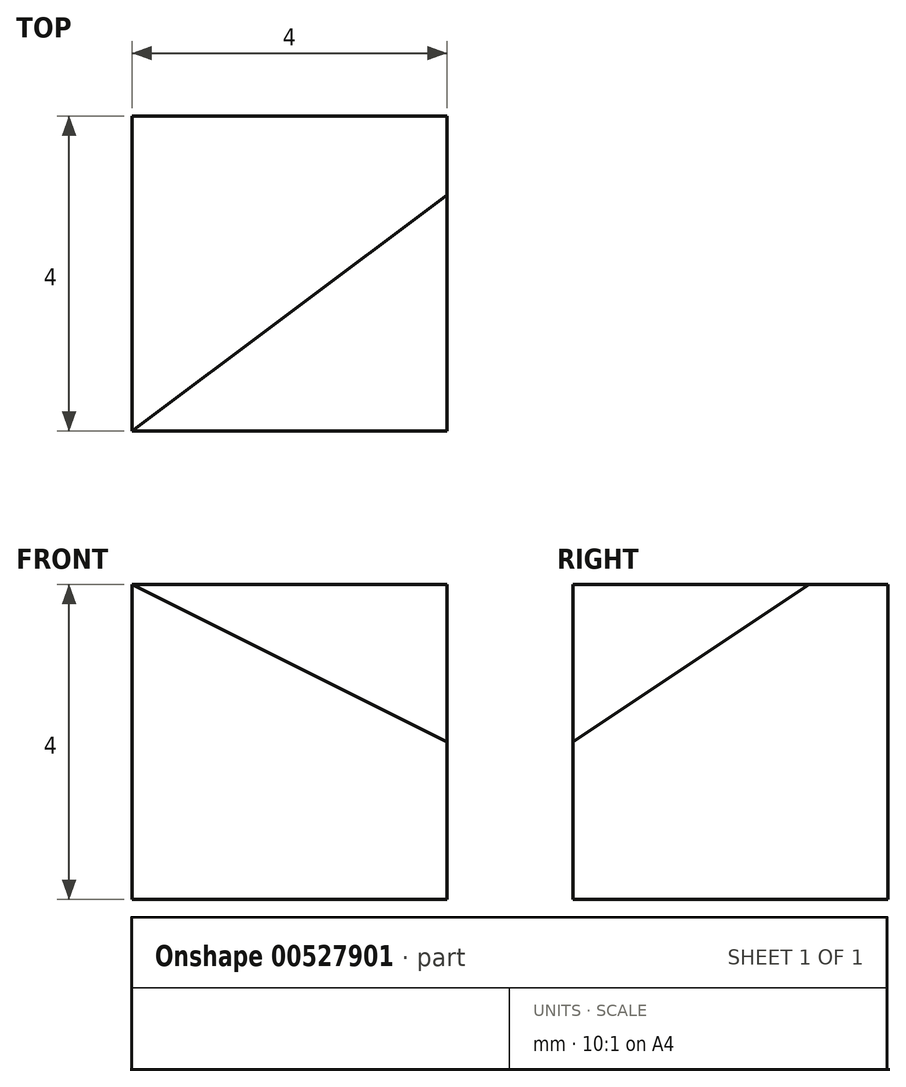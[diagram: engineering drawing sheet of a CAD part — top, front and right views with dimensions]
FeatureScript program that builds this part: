
annotation { "Feature Type Name" : "Feature", "Feature Type Description" : "" }
export const myFeature = defineFeature(function(context is Context, id is Id, definition is map)
    precondition{}
    {
        {
            var Q0;
            Q0=qCreatedBy(makeId("Top.planeOp"),FACE);
            var sketch = newSketch(context, id + "F0", { "sketchPlane" : qUnion([Q0])});
            skLineSegment(sketch, "E0.bottom", {"start": v(0, 0) * mm, "end": v(4, 0) * mm});
            skLineSegment(sketch, "E0.top", {"start": v(0, 4) * mm, "end": v(4, 4) * mm});
            skLineSegment(sketch, "E0.left", {"start": v(0, 0) * mm, "end": v(0, 4) * mm});
            skLineSegment(sketch, "E0.right", {"start": v(4, 0) * mm, "end": v(4, 4) * mm});
            skSolve(sketch);
        }
        {
            var Q0;
            Q0=qSketchRegion(id+"F0",true);
            extrude(context, id + "F1", {"entities" : qUnion([Q0]), "depth" : 4 * mm});
        }
        {
            var Q0;
            Q0=makeQuery(id+"F1.opExtrude","SWEPT_FACE",FACE,{"disambiguationData":[OSD([sQuery(id+"F0.wireOp",EDGE,"E0.bottom")])]});
            var sketch = newSketch(context, id + "F2", { "sketchPlane" : qUnion([Q0])});
            skLineSegment(sketch, "E1", {"start": v(4, 0) * mm, "end": v(4, 2) * mm, "construction": true});
            skSolve(sketch);
        }
        {
            var Q0;
            Q0=makeQuery(id+"F1.opExtrude","SWEPT_FACE",FACE,{"disambiguationData":[OSD([sQuery(id+"F0.wireOp",EDGE,"E0.right")])]});
            var sketch = newSketch(context, id + "F3", { "sketchPlane" : qUnion([Q0])});
            skLineSegment(sketch, "E2", {"start": v(4, 4) * mm, "end": v(3, 4) * mm, "construction": true});
            skSolve(sketch);
        }
        {
            var Q0;
            Q0=makeQuery(id+"F1.opExtrude","CAP_VERTEX",VERTEX,{"disambiguationData":[OSD([sQuery(id+"F0.wireOp",EDGE,"E0.bottom"),sQuery(id+"F0.wireOp",EDGE,"E0.left")])],"isStart":false});
            var Q1;
            Q1=sQuery(id+"F3.wireOp",VERTEX,"E2.end");
            var Q2;
            Q2=sQuery(id+"F2.wireOp",VERTEX,"E1.end");
            cPlane(context, id + "F4", {"entities" : qUnion([Q0, Q1, Q2]), "cplaneType" : CPlaneType.THREE_POINT, "offset" : 25 * mm, "width" : 150 * mm, "height" : 150 * mm});
        }
        {
            var Q0;
            Q0=qCreatedBy(id+"F4.planeOp",FACE);
            var sketch = newSketch(context, id + "F5", { "sketchPlane" : qUnion([Q0])});
            skPoint(sketch, "E3.0", {"position": v(-1.28, 2.22) * mm});
            skPoint(sketch, "E3.1", {"position": v(3.05, 4.71) * mm});
            skPoint(sketch, "E3.2", {"position": v(3.05, 1.1) * mm});
            skLineSegment(sketch, "E4", {"start": v(-1.28, 2.22) * mm, "end": v(3.05, 4.71) * mm});
            skLineSegment(sketch, "E5", {"start": v(3.05, 1.1) * mm, "end": v(3.05, 4.71) * mm});
            skLineSegment(sketch, "E6", {"start": v(3.05, 1.1) * mm, "end": v(-1.28, 2.22) * mm});
            skSolve(sketch);
        }
        {
            var Q0;
            Q0=qSketchRegion(id+"F5",true);
            extrude(context, id + "F6", {"entities" : qUnion([Q0]), "operationType" : NewBodyOperationType.REMOVE, "depth" : 25 * mm});
        }
    });
